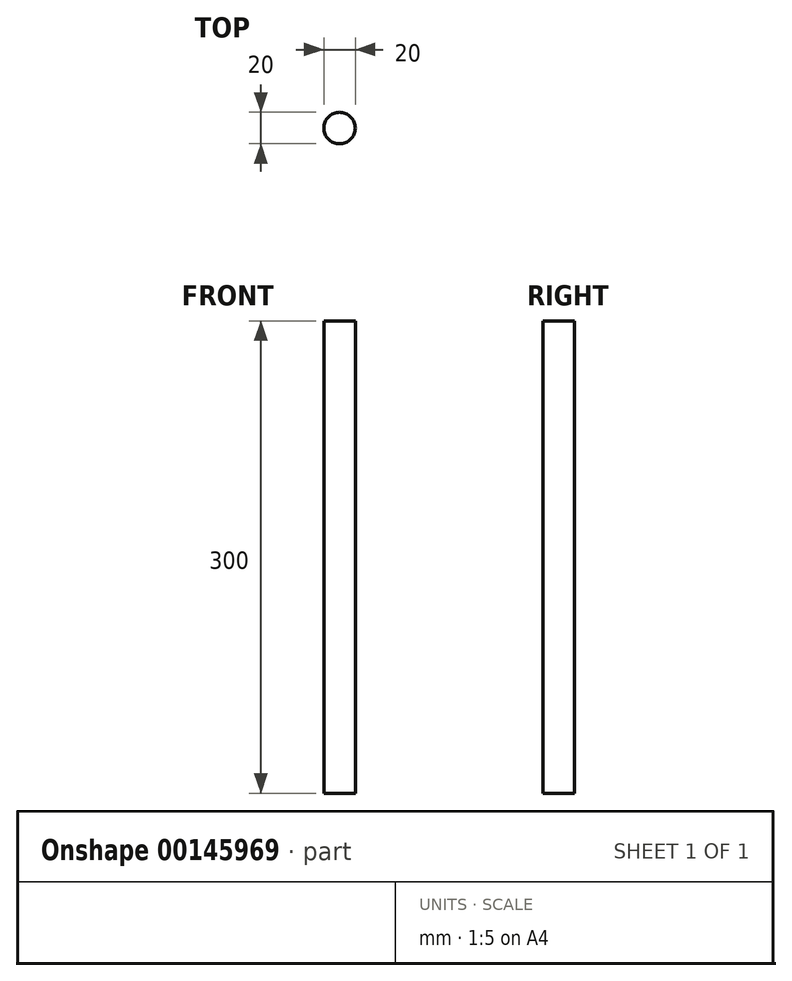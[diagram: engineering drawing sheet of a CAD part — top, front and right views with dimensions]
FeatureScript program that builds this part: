
annotation { "Feature Type Name" : "Feature", "Feature Type Description" : "" }
export const myFeature = defineFeature(function(context is Context, id is Id, definition is map)
    precondition{}
    {
        {
            var Q0;
            Q0=qCreatedBy(makeId("Top.planeOp"),FACE);
            var sketch = newSketch(context, id + "F0", { "sketchPlane" : qUnion([Q0])});
            skCircle(sketch, "E0", {"center": v(0, 0) * mm, "radius": 10 * mm});
            skSolve(sketch);
        }
        {
            var Q0;
            Q0=makeQuery(id+"F0.imprint","IMPRINT",FACE,{"disambiguationData":[TD([[makeQuery(id+"F0.imprint","IMPRINT",EDGE,{"derivedFrom":sQuery(id+"F0.wireOp",EDGE,"E0")}),1.0]])]});
            extrude(context, id + "F1", {"entities" : qUnion([Q0]), "depth" : 300 * mm});
        }
    });
